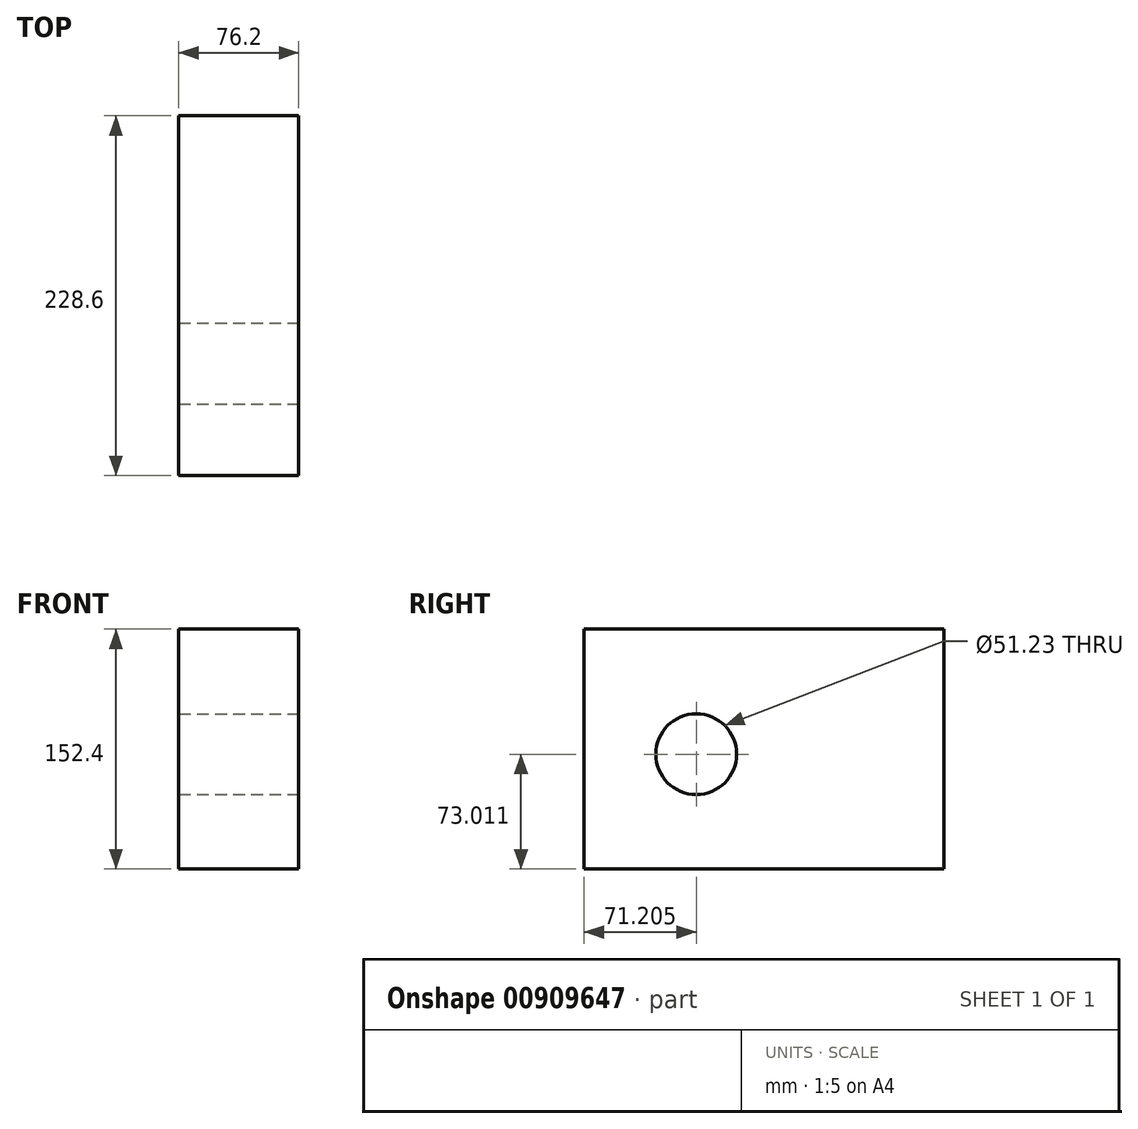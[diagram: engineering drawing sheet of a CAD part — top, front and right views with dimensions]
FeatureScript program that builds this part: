
annotation { "Feature Type Name" : "Feature", "Feature Type Description" : "" }
export const myFeature = defineFeature(function(context is Context, id is Id, definition is map)
    precondition{}
    {
        {
            var Q0;
            Q0=qCreatedBy(makeId("Right.planeOp"),FACE);
            var sketch = newSketch(context, id + "F0", { "sketchPlane" : qUnion([Q0])});
            skLineSegment(sketch, "E0", {"start": v(-228.6, 152.4) * mm, "end": v(0, 152.4) * mm});
            skLineSegment(sketch, "E1", {"start": v(0, 152.4) * mm, "end": v(0, 0) * mm});
            skLineSegment(sketch, "E2", {"start": v(-228.6, 152.4) * mm, "end": v(-228.6, 0) * mm});
            skLineSegment(sketch, "E3", {"start": v(-228.6, 0) * mm, "end": v(0, 0) * mm});
            skSolve(sketch);
        }
        {
            var Q0;
            Q0=makeQuery(id+"F0.imprint","IMPRINT",FACE,{"disambiguationData":[TD([[makeQuery(id+"F0.imprint","IMPRINT",EDGE,{"derivedFrom":sQuery(id+"F0.wireOp",EDGE,"E0")}),-1.0]])]});
            extrude(context, id + "F1", {"entities" : qUnion([Q0]), "depth" : 76.2 * mm, "offsetDistance" : 25.4 * mm});
        }
        {
            var Q0;
            Q0=makeQuery(id+"F1.opExtrude","CAP_FACE",FACE,{"disambiguationData":[OSD([sQuery(id+"F0.wireOp",EDGE,"E0"),sQuery(id+"F0.wireOp",EDGE,"E1"),sQuery(id+"F0.wireOp",EDGE,"E2"),sQuery(id+"F0.wireOp",EDGE,"E3")])],"isStart":false});
            var sketch = newSketch(context, id + "F2", { "sketchPlane" : qUnion([Q0])});
            skCircle(sketch, "E4", {"center": v(-157.4, 73.01) * mm, "radius": 25.61 * mm});
            skSolve(sketch);
        }
        {
            var Q0;
            Q0=makeQuery(id+"F2.imprint","IMPRINT",FACE,{"disambiguationData":[TD([[makeQuery(id+"F2.imprint","IMPRINT",EDGE,{"derivedFrom":sQuery(id+"F2.wireOp",EDGE,"E4")}),1.0]])]});
            extrude(context, id + "F3", {"entities" : qUnion([Q0]), "operationType" : NewBodyOperationType.REMOVE, "oppositeDirection" : true, "depth" : 76.2 * mm, "offsetDistance" : 25.4 * mm});
        }
    });
